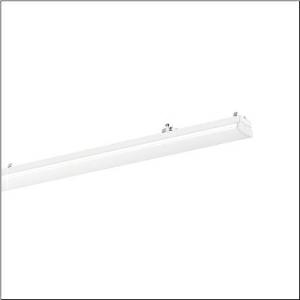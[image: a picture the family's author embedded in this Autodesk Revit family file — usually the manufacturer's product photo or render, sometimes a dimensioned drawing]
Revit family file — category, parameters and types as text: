
# Revit family: licross_21_recessed_opal_mo_52te1dvn48xg
name_source: partatom
category: Lighting Fixtures
units: mm (PartAtom-declared; Revit-internal decimal feet)

## family parameters
Cut with Voids When Loaded = No
Host = Face
Light Source = No
Part Type = Normal
Room Calculation Point = No
Round Connector Dimension = Use Diameter
Shared = No

## types (1)
- --- (1 x LED, 8000 lm, 46.8 W, 4000K)
    Apparent Load = 47 VA
    CIE Flux Codes = 44 73 91 87 100
    Color Rendering = 80
    Color Temperature = 4000K
    Default Elevation = 1800 mm
    Description = Licross 21 recessed opal MO, luminaire insert, of sheet steel, galvanised, coil coated, white, length: 1.500mm, width: 66mm, height: 67mm, LED rated luminous flux: 8.000lm, light colour: 840, SDCM (Standard Deviation of Colour Matching)MacAdam ≤ 3 SDCM (initial), control gear: DALI 2, CLO, with plug, 5-pole, with phase selection, mains connection: 220..240V, AC, 50/60Hz, start of lifetime: 47W, end of service life: 56W, internal wiring halogen-free, primary optical cover: cover, of PMMA, light emission: direct with ceiling illumination distribution, primary light characteristic: symmetric, protection rating (complete): IP54, insulation class (complete): insulation class I (protective earthing), certification: CE, ENEC, VDE, UKCA, protection symbol: D if used in an environment with non-conductive dust loads with corresponding accessories, impact resistance: IK06, permissible ambient temperature for indoor applications: -25..+35°C, corresponds to IFS (International Featured Standards) requirements for safety and quality in the food industry, reducing of maximum allowable ambient temperature of 5°C with ceiling mounting, LABS conformity tested according to VDMA 24364:2018-05, The light source and the operating device comply with the requirements of the Ecodesign Regulation (EU) 2019/2020 and are replaceable in accordance with this regulation, packaging unit: 1 piece
    Height = 83 mm
    Lamp = 1 x LED
    Lamp Light Flux = 8000 lm
    Lamp Power = 46.8 W
    Lamp count = 1
    Length = 1500 mm
    Luminous efficacy = 171 lm/W
    Manufacturer = Siteco
    ModVariant = No
    Model = 52TE1DVN48XG
    Mounting Place = Ceiling
    Mounting Type = Pendant
    Number of Poles = 1
    OnlyDefault = Yes
    Power Factor = 1
    Product Name = Licross 21 recessed opal MO
    Product group = luminaire insert | ceiling pendant
    ProductGroupID = 901
    Protection Class = Protection class I
    Protection Degree = IP 54
    RLX_Detail_Level = 1
    RLX_Emergency_Light_Flux = 0 lm
    RLX_Emergency_Type = 0
    RLX_Emergency_Type_DB = No
    RlxData = <blob elided: 27293 chars, md5=a5d5c139>
    Socket = socket
    Standby Power = 0 W
    System Light Flux = 8000 lm
    System Power = 47 W
    Type Comments = factory setting: luminous flux: 100 % | dim-lin: 254 | 315 mA
    Type Image = l_1313666.jpg
    URL = http://relux.com
    VarID = @adj_076085
    Voltage = 0 V
    Weight = 0.00 kg
    Width = 76 mm

## geometry (parser evidence)
native form markers: Blend x4, Sweep x12
no freeform markers — native parametric forms only
